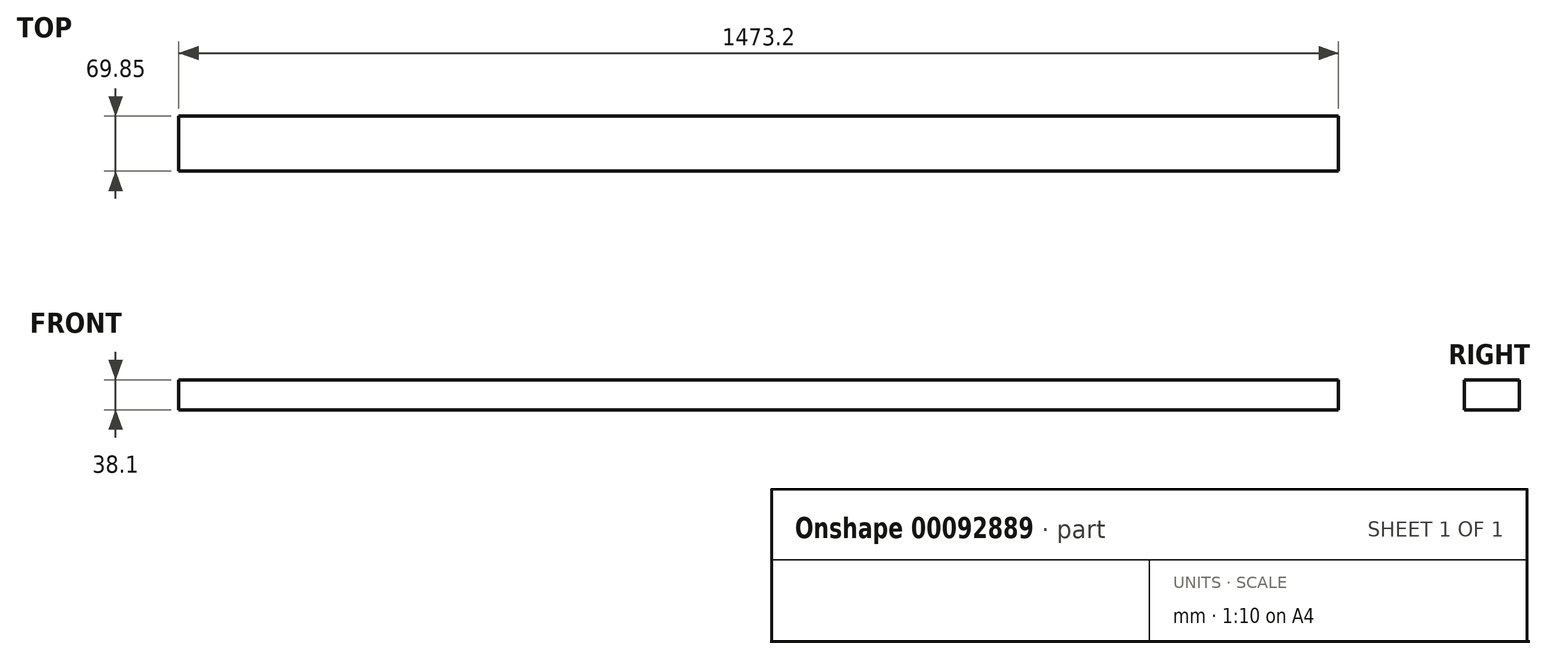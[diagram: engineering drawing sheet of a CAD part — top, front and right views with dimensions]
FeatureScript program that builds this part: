
annotation { "Feature Type Name" : "Feature", "Feature Type Description" : "" }
export const myFeature = defineFeature(function(context is Context, id is Id, definition is map)
    precondition{}
    {
        {
            var Q0;
            Q0=qCreatedBy(makeId("Front.planeOp"),FACE);
            var sketch = newSketch(context, id + "F0", { "sketchPlane" : qUnion([Q0])});
            skLineSegment(sketch, "E0.bottom", {"start": v(-766.06, -2.83) * mm, "end": v(707.14, -2.83) * mm});
            skLineSegment(sketch, "E0.top", {"start": v(-766.06, -40.93) * mm, "end": v(707.14, -40.93) * mm});
            skLineSegment(sketch, "E0.left", {"start": v(-766.06, -2.83) * mm, "end": v(-766.06, -40.93) * mm});
            skLineSegment(sketch, "E0.right", {"start": v(707.14, -2.83) * mm, "end": v(707.14, -40.93) * mm});
            skSolve(sketch);
        }
        {
            var Q0;
            Q0=makeQuery(id+"F0.imprint","IMPRINT",FACE,{"disambiguationData":[TD([[makeQuery(id+"F0.imprint","IMPRINT",EDGE,{"derivedFrom":sQuery(id+"F0.wireOp",EDGE,"E0.bottom")}),-1.0]])]});
            extrude(context, id + "F1", {"entities" : qUnion([Q0]), "depth" : 69.85 * mm});
        }
    });
